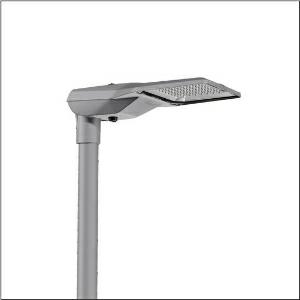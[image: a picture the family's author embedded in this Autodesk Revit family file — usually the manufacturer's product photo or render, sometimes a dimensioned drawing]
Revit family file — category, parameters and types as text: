
# Revit family: streetlight_sl_21_iq_midi___st1_0a_5xe3d21y08nb_2a15
name_source: partatom
category: Lighting Fixtures
units: mm (PartAtom-declared; Revit-internal decimal feet)

## family parameters
Cut with Voids When Loaded = No
Host = Face
Light Source = No
Part Type = Normal
Room Calculation Point = No
Round Connector Dimension = Use Diameter
Shared = No

## types (1)
- --- (1 x LED, 17280 lm, 136.6 W, 2200K)
    Apparent Load = 137 VA
    CIE Flux Codes = 40 73 97 100 100
    Color Rendering = 70
    Color Temperature = 2200K
    Default Elevation = 1800 mm
    Description = Streetlight SL 21 iQ midi, mast luminaire, primary light control with lens, of PMMA, primary optical cover: cover, of toughened safety glass, transparent, light distribution: ST1.0a, light emission: direct distribution, primary light characteristic: asymmetric, installation type: post-top, side-entry, LED, High Power LED, rated luminous flux: 17.280lm, luminous efficacy: 127lm/W, light colour: 722, colour temperature: 2200K, control gear: iQ-Street Remote, D4i with power reduction, control: pre-setting: logarithmic dimming characteristic, Street-Remote, Auto-Match, Temp-Guard, Lumen-Switch, Night-Set, Smart-Wire, Light-Fading, Desk-Remote (wireless, voltage-free reading and setting of iQ features in the workshop via application-optimized NFC function/RFID function), optimised constant luminous flux control (CLO 2.0), mains connection: 230..240V, AC, 50/60Hz, start of lifetime: 137W, end of service life: 144W, reduction: 61W, luminaire housing, of diecast aluminium, powder-coated, Siteco® metallic grey (DB 702S), corrosivity category C5 mid according to DIN EN ISO 12944, please order mast flange separately, inclination adjustable: 0°, 5°, 10°, 15°, sealing non-destructively replaceable, multi-level sealing system, length: 644mm, width: 335mm, height: 110mm, mast flange for spigot size: 42mm (side-entry): 5XC10008XM4, 60/48mm (side-entry/post-top): 5XC10108XM2, 76/60mm (side-entry/post-top): 5XC10108XM1, mounting height: 4..8m, Smart Interface below and above, protection rating (complete): IP66, insulation class (complete): insulation class II (safety insulation), certification: CE, ENEC, ENEC+, VDE, impact resistance: IK10, permissible operating ambient temperature for outdoor applications: -40..+50°C, standard-compliant lighting for roads and squares, packaging unit: 1 piece

Light Distribution: ST1.0a
    Height = 111 mm
    Lamp = 1 x LED
    Lamp Light Flux = 17280 lm
    Lamp Power = 136.6 W
    Lamp count = 1
    Length = 644 mm
    Luminous efficacy = 127 lm/W
    Manufacturer = Siteco
    ModVariant = No
    Model = 5XE3D21Y08NB
    Number of Poles = 1
    OnlyDefault = Yes
    Power Factor = 1
    Product Name = Streetlight SL 21 iQ midi | ST1.0a
    Product group = mast luminaire | pylon top
    ProductGroupID = 6100
    Protection Class = Protection class II
    Protection Degree = IP 66
    RLX_Detail_Level = 1
    RLX_Emergency_Light_Flux = 0 lm
    RLX_Emergency_Type = 0
    RLX_Emergency_Type_DB = No
    RlxData = <blob elided: 27341 chars, md5=28098b8b>
    Socket = socket
    Standby Power = 0 W
    System Light Flux = 17280 lm
    System Power = 137 W
    Type Comments = factory setting: luminous flux: 100 % | dim-lin: 254 | 733 mA
    Type Image = l_1004304.jpg
    URL = http://relux.com
    VarID = @adj_113882
    Voltage = 0 V
    Weight = 0.00 kg
    Width = 336 mm

## geometry (parser evidence)
native form markers: Blend x4, Sweep x12
no freeform markers — native parametric forms only
